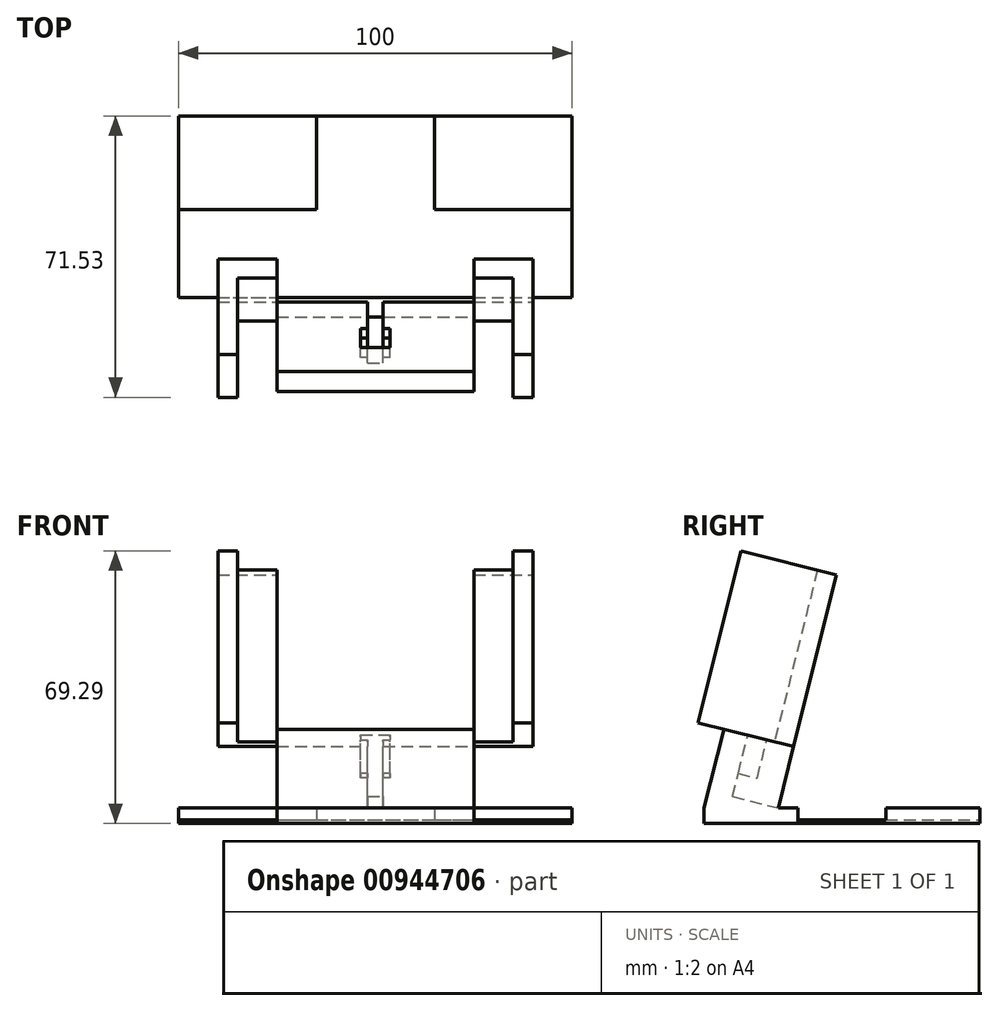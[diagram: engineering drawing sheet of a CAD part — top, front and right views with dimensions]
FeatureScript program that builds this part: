
annotation { "Feature Type Name" : "Feature", "Feature Type Description" : "" }
export const myFeature = defineFeature(function(context is Context, id is Id, definition is map)
    precondition{}
    {
        {
            var Q0;
            Q0=qCreatedBy(makeId("Top.planeOp"),FACE);
            var sketch = newSketch(context, id + "F0", { "sketchPlane" : qUnion([Q0])});
            skLineSegment(sketch, "E0.bottom", {"start": v(-50, 0) * mm, "end": v(50, 0) * mm});
            skLineSegment(sketch, "E0.top", {"start": v(-50, 70) * mm, "end": v(50, 70) * mm});
            skLineSegment(sketch, "E0.left", {"start": v(-50, 0) * mm, "end": v(-50, 70) * mm});
            skLineSegment(sketch, "E0.right", {"start": v(50, 0) * mm, "end": v(50, 70) * mm});
            skLineSegment(sketch, "E1.top", {"start": v(-15, 70) * mm, "end": v(15, 70) * mm});
            skLineSegment(sketch, "E1.left", {"start": v(-15, 46.16) * mm, "end": v(-15, 70) * mm});
            skLineSegment(sketch, "E1.right", {"start": v(15, 46.16) * mm, "end": v(15, 70) * mm});
            skLineSegment(sketch, "E2.bottom", {"start": v(-50, 46.16) * mm, "end": v(-15, 46.16) * mm});
            skLineSegment(sketch, "E2.top", {"start": v(-50, 23.84) * mm, "end": v(50, 23.84) * mm});
            skLineSegment(sketch, "E2.left", {"start": v(-50, 46.16) * mm, "end": v(-50, 23.84) * mm});
            skLineSegment(sketch, "E2.right", {"start": v(50, 46.16) * mm, "end": v(50, 23.84) * mm});
            skPoint(sketch, "E3", {"position": v(50, 35) * mm});
            skPoint(sketch, "E4", {"position": v(0, 70) * mm});
            skLineSegment(sketch, "E5.trimOffspring", {"start": v(15, 46.16) * mm, "end": v(50, 46.16) * mm});
            skLineSegment(sketch, "E6.bottom", {"start": v(-25, 0) * mm, "end": v(25, 0) * mm});
            skLineSegment(sketch, "E6.top", {"start": v(-25, 23.84) * mm, "end": v(25, 23.84) * mm});
            skLineSegment(sketch, "E6.left", {"start": v(-25, 0) * mm, "end": v(-25, 23.84) * mm});
            skLineSegment(sketch, "E6.right", {"start": v(25, 0) * mm, "end": v(25, 23.84) * mm});
            skSolve(sketch);
        }
        {
            var Q0;
            {var subQ0=sQuery(id+"F0.wireOp",EDGE,"E1.left");Q0=makeQuery(id+"F0.imprint","IMPRINT",FACE,{"disambiguationData":[TD([[makeQuery(id+"F0.imprint","IMPRINT",EDGE,{"derivedFrom":subQ0}),-1.0]])]});}
            extrude(context, id + "F1", {"entities" : qUnion([Q0]), "depth" : 1 * mm, "offsetDistance" : 25 * mm});
        }
        {
            var Q0;
            {var subQ0=sQuery(id+"F0.wireOp",EDGE,"E6.left");Q0=makeQuery(id+"F0.imprint","IMPRINT",FACE,{"disambiguationData":[TD([[makeQuery(id+"F0.imprint","IMPRINT",EDGE,{"derivedFrom":subQ0}),-1.0]])]});}
            var Q1;
            {var subQ0=sQuery(id+"F0.wireOp",EDGE,"E1.right");Q1=makeQuery(id+"F0.imprint","IMPRINT",FACE,{"disambiguationData":[TD([[makeQuery(id+"F0.imprint","IMPRINT",EDGE,{"derivedFrom":subQ0}),-1.0]])]});}
            var Q2;
            {var subQ3=sQuery(id+"F0.wireOp",EDGE,"E1.left");Q2=makeQuery(id+"F0.imprint","IMPRINT",FACE,{"disambiguationData":[TD([[makeQuery(id+"F0.imprint","IMPRINT",EDGE,{"derivedFrom":subQ3}),1.0]])]});}
            extrude(context, id + "F2", {"entities" : qUnion([Q0, Q1, Q2]), "operationType" : NewBodyOperationType.ADD, "depth" : 4 * mm, "offsetDistance" : 25 * mm});
        }
        {
            var Q0;
            Q0=makeQuery(id+"F2.opExtrude","CAP_FACE",FACE,{"disambiguationData":[OSD([sQuery(id+"F0.wireOp",EDGE,"E0.bottom"),sQuery(id+"F0.wireOp",EDGE,"E2.top"),sQuery(id+"F0.wireOp",EDGE,"E6.left"),sQuery(id+"F0.wireOp",EDGE,"E6.right")])],"isStart":false});
            var sketch = newSketch(context, id + "F3", { "sketchPlane" : qUnion([Q0])});
            skLineSegment(sketch, "E7.bottom", {"start": v(-25, 0) * mm, "end": v(25, 0) * mm});
            skLineSegment(sketch, "E7.top", {"start": v(-25, 18.84) * mm, "end": v(25, 18.84) * mm});
            skLineSegment(sketch, "E7.left", {"start": v(-25, 0) * mm, "end": v(-25, 18.84) * mm});
            skLineSegment(sketch, "E7.right", {"start": v(25, 0) * mm, "end": v(25, 18.84) * mm});
            skLineSegment(sketch, "E8.bottom", {"start": v(-25, 23.84) * mm, "end": v(25, 23.84) * mm});
            skLineSegment(sketch, "E8.top", {"start": v(-25, 5) * mm, "end": v(25, 5) * mm});
            skLineSegment(sketch, "E8.left", {"start": v(-25, 23.84) * mm, "end": v(-25, 5) * mm});
            skLineSegment(sketch, "E8.right", {"start": v(25, 23.84) * mm, "end": v(25, 5) * mm});
            skSolve(sketch);
        }
        {
            var Q0;
            {var subQ0=sQuery(id+"F3.wireOp",EDGE,"E7.top");Q0=makeQuery(id+"F3.imprint","IMPRINT",FACE,{"disambiguationData":[TD([[makeQuery(id+"F3.imprint","IMPRINT",EDGE,{"derivedFrom":subQ0}),1.0]])]});}
            var Q1;
            {var subQ0=sQuery(id+"F3.wireOp",EDGE,"E7.top");Q1=makeQuery(id+"F3.imprint","IMPRINT",FACE,{"disambiguationData":[TD([[makeQuery(id+"F3.imprint","IMPRINT",EDGE,{"derivedFrom":subQ0}),-1.0]])]});}
            var Q2;
            Q2=makeQuery(id+"F3.imprint","IMPRINT",FACE,{"disambiguationData":[TD([[makeQuery(id+"F3.imprint","IMPRINT",EDGE,{"derivedFrom":sQuery(id+"F3.wireOp",EDGE,"E7.bottom")}),1.0]])]});
            extrude(context, id + "F4", {"entities" : qUnion([Q0, Q1, Q2]), "operationType" : NewBodyOperationType.ADD, "depth" : 20 * mm, "offsetDistance" : 25 * mm});
        }
        {
            var Q0;
            Q0=makeQuery(id+"F4.boolean.opBoolean","MERGE",FACE,{"derivedFrom":[makeQuery(id+"F2.opExtrude","SWEPT_FACE",FACE,{"disambiguationData":[OSD([sQuery(id+"F0.wireOp",EDGE,"E6.right")])]}),makeQuery(id+"F4.opExtrude","SWEPT_FACE",FACE,{"disambiguationData":[OSD([sQuery(id+"F3.wireOp",EDGE,"E7.right"),sQuery(id+"F3.wireOp",EDGE,"E8.right")])]})]});
            var sketch = newSketch(context, id + "F5", { "sketchPlane" : qUnion([Q0])});
            skLineSegment(sketch, "E9.0", {"start": v(0, 4) * mm, "end": v(18.84, 4) * mm});
            skLineSegment(sketch, "E9.1", {"start": v(23.84, 4) * mm, "end": v(5, 4) * mm});
            skLineSegment(sketch, "E10", {"start": v(5, 4) * mm, "end": v(5, 24) * mm, "construction": true});
            skLineSegment(sketch, "E11", {"start": v(0, 4) * mm, "end": v(5, 24) * mm});
            skLineSegment(sketch, "E12", {"start": v(18.84, 4) * mm, "end": v(23.84, 24) * mm});
            skLineSegment(sketch, "E13", {"start": v(5, 24) * mm, "end": v(22.73, 19.57) * mm});
            skSolve(sketch);
        }
        {
            var Q0;
            {var subQ0=sQuery(id+"F5.wireOp",EDGE,"E11");Q0=makeQuery(id+"F5.imprint","IMPRINT",FACE,{"disambiguationData":[TD([[makeQuery(id+"F5.imprint","IMPRINT",EDGE,{"derivedFrom":subQ0}),1.0]])]});}
            var Q1;
            {var subQ0=sQuery(id+"F5.wireOp",EDGE,"E9.1");Q1=makeQuery(id+"F5.imprint","IMPRINT",FACE,{"disambiguationData":[TD([[makeQuery(id+"F5.imprint","IMPRINT",EDGE,{"derivedFrom":subQ0}),-1.0]])]});}
            var Q2;
            {var subQ6=sQuery(id+"F5.wireOp",EDGE,"E13");Q2=makeQuery(id+"F5.imprint","IMPRINT",FACE,{"disambiguationData":[TD([[makeQuery(id+"F5.imprint","IMPRINT",EDGE,{"derivedFrom":subQ6}),1.0]])]});}
            extrude(context, id + "F6", {"entities" : qUnion([Q0, Q1, Q2]), "operationType" : NewBodyOperationType.REMOVE, "oppositeDirection" : true, "depth" : 50 * mm, "offsetDistance" : 25 * mm});
        }
        {
            var Q0;
            Q0=makeQuery(id+"F6.boolean.opBoolean","COPY",FACE,{"derivedFrom":makeQuery(id+"F6.opExtrude","SWEPT_FACE",FACE,{"disambiguationData":[OSD([sQuery(id+"F5.wireOp",EDGE,"E12")])]})});
            var sketch = newSketch(context, id + "F7", { "sketchPlane" : qUnion([Q0])});
            skLineSegment(sketch, "E14.bottom", {"start": v(-3.75, 8.45) * mm, "end": v(3.75, 8.45) * mm});
            skLineSegment(sketch, "E14.top", {"start": v(-3.75, 24.5) * mm, "end": v(3.75, 24.5) * mm});
            skLineSegment(sketch, "E14.left", {"start": v(-3.75, 8.45) * mm, "end": v(-3.75, 24.5) * mm});
            skLineSegment(sketch, "E14.right", {"start": v(3.75, 8.45) * mm, "end": v(3.75, 24.5) * mm});
            skPoint(sketch, "E15", {"position": v(0, 8.45) * mm});
            skLineSegment(sketch, "E16.bottom", {"start": v(-2, 8.45) * mm, "end": v(2, 8.45) * mm});
            skLineSegment(sketch, "E16.top", {"start": v(-2, 24.5) * mm, "end": v(2, 24.5) * mm});
            skLineSegment(sketch, "E16.left", {"start": v(-2, 8.45) * mm, "end": v(-2, 24.5) * mm});
            skLineSegment(sketch, "E16.right", {"start": v(2, 8.45) * mm, "end": v(2, 24.5) * mm});
            skLineSegment(sketch, "E17.bottom", {"start": v(-3.75, 14.5) * mm, "end": v(3.75, 14.5) * mm});
            skLineSegment(sketch, "E17.left", {"start": v(-3.75, 14.5) * mm, "end": v(-3.75, 24.5) * mm});
            skLineSegment(sketch, "E17.right", {"start": v(3.75, 14.5) * mm, "end": v(3.75, 24.5) * mm});
            skSolve(sketch);
        }
        {
            var Q0;
            {var subQ0=sQuery(id+"F7.wireOp",EDGE,"E16.right");var subQ1=sQuery(id+"F7.wireOp",EDGE,"E14.top");var subQ2=makeQuery(id+"F7.imprint","INTERSECT",VERTEX,{"derivedFrom":[subQ1,subQ0]});Q0=makeQuery(id+"F7.imprint","IMPRINT",FACE,{"disambiguationData":[TD([[makeQuery(id+"F7.imprint","IMPRINT",EDGE,{"disambiguationData":[TD([[subQ2,-1.0]])],"derivedFrom":subQ1}),1.0]])]});}
            var Q1;
            {var subQ0=sQuery(id+"F7.wireOp",EDGE,"E16.right");var subQ1=sQuery(id+"F7.wireOp",EDGE,"E14.bottom");var subQ2=makeQuery(id+"F7.imprint","INTERSECT",VERTEX,{"derivedFrom":[subQ1,subQ0]});Q1=makeQuery(id+"F7.imprint","IMPRINT",FACE,{"disambiguationData":[TD([[makeQuery(id+"F7.imprint","IMPRINT",EDGE,{"disambiguationData":[TD([[subQ2,-1.0]])],"derivedFrom":subQ1}),-1.0]])]});}
            extrude(context, id + "F8", {"entities" : qUnion([Q0, Q1]), "operationType" : NewBodyOperationType.REMOVE, "oppositeDirection" : true, "depth" : 12 * mm, "offsetDistance" : 25 * mm});
        }
        {
            var Q0;
            {var subQ3=sQuery(id+"F7.wireOp",EDGE,"E16.right");var subQ5=sQuery(id+"F7.wireOp",EDGE,"E17.bottom");var subQ7=makeQuery(id+"F7.imprint","INTERSECT",VERTEX,{"derivedFrom":[subQ3,subQ5]});Q0=makeQuery(id+"F7.imprint","IMPRINT",FACE,{"disambiguationData":[TD([[makeQuery(id+"F7.imprint","IMPRINT",EDGE,{"disambiguationData":[TD([[subQ7,-1.0]])],"derivedFrom":subQ3}),-1.0]])]});}
            var Q1;
            {var subQ3=sQuery(id+"F7.wireOp",EDGE,"E16.left");var subQ5=sQuery(id+"F7.wireOp",EDGE,"E17.bottom");var subQ6=makeQuery(id+"F7.imprint","INTERSECT",VERTEX,{"derivedFrom":[subQ3,subQ5]});Q1=makeQuery(id+"F7.imprint","IMPRINT",FACE,{"disambiguationData":[TD([[makeQuery(id+"F7.imprint","IMPRINT",EDGE,{"disambiguationData":[TD([[subQ6,-1.0]])],"derivedFrom":subQ3}),1.0]])]});}
            extrude(context, id + "F9", {"entities" : qUnion([Q0, Q1]), "operationType" : NewBodyOperationType.REMOVE, "oppositeDirection" : true, "depth" : 12 * mm, "offsetDistance" : 25 * mm, "hasSecondDirection" : true, "secondDirectionOppositeDirection" : true, "secondDirectionDepth" : 7 * mm});
        }
        {
            var Q0;
            Q0=makeQuery(id+"F6.boolean.opBoolean","COPY",FACE,{"derivedFrom":makeQuery(id+"F6.opExtrude","SWEPT_FACE",FACE,{"disambiguationData":[OSD([sQuery(id+"F5.wireOp",EDGE,"E13")])]})});
            var sketch = newSketch(context, id + "F10", { "sketchPlane" : qUnion([Q0])});
            skPoint(sketch, "E18", {"position": v(0, 17.3) * mm});
            skLineSegment(sketch, "E19", {"start": v(-40, 17.3) * mm, "end": v(40, 17.3) * mm});
            skLineSegment(sketch, "E20", {"start": v(40, 17.3) * mm, "end": v(40, -7.7) * mm});
            skLineSegment(sketch, "E21", {"start": v(40, -7.7) * mm, "end": v(35, -7.7) * mm});
            skLineSegment(sketch, "E22", {"start": v(35, -7.7) * mm, "end": v(35, 12.3) * mm});
            skLineSegment(sketch, "E23", {"start": v(35, 12.3) * mm, "end": v(-35, 12.3) * mm});
            skLineSegment(sketch, "E24", {"start": v(-35, 12.3) * mm, "end": v(-35, -7.7) * mm});
            skLineSegment(sketch, "E25", {"start": v(-35, -7.7) * mm, "end": v(-40, -7.7) * mm});
            skLineSegment(sketch, "E26", {"start": v(-40, -7.7) * mm, "end": v(-40, 17.3) * mm});
            skSolve(sketch);
        }
        {
            var Q0;
            {var subQ1=sQuery(id+"F10.wireOp",EDGE,"E20");Q0=makeQuery(id+"F10.imprint","IMPRINT",FACE,{"disambiguationData":[TD([[makeQuery(id+"F10.imprint","IMPRINT",EDGE,{"derivedFrom":subQ1}),-1.0]])]});}
            var Q1;
            {var subQ0=sQuery(id+"F10.wireOp",EDGE,"E19");var subQ1=makeQuery(id+"F6.boolean.opBoolean","COPY",EDGE,{"derivedFrom":makeQuery(id+"F6.opExtrude","CAP_EDGE",EDGE,{"disambiguationData":[OSD([sQuery(id+"F5.wireOp",EDGE,"E13")])],"isStart":true})});var subQ2=makeQuery(id+"F10.imprint","INTERSECT",VERTEX,{"derivedFrom":[subQ1,subQ0]});Q1=makeQuery(id+"F10.imprint","IMPRINT",FACE,{"disambiguationData":[TD([[makeQuery(id+"F10.imprint","IMPRINT",EDGE,{"disambiguationData":[TD([[subQ2,1.0]])],"derivedFrom":subQ1}),1.0]])]});}
            var Q2;
            {var subQ0=sQuery(id+"F10.wireOp",EDGE,"E19");var subQ1=makeQuery(id+"F6.boolean.opBoolean","COPY",EDGE,{"derivedFrom":makeQuery(id+"F6.opExtrude","CAP_EDGE",EDGE,{"disambiguationData":[OSD([sQuery(id+"F5.wireOp",EDGE,"E13")])],"isStart":false})});var subQ2=makeQuery(id+"F10.imprint","INTERSECT",VERTEX,{"derivedFrom":[subQ1,subQ0]});Q2=makeQuery(id+"F10.imprint","IMPRINT",FACE,{"disambiguationData":[TD([[makeQuery(id+"F10.imprint","IMPRINT",EDGE,{"disambiguationData":[TD([[subQ2,1.0]])],"derivedFrom":subQ1}),-1.0]])]});}
            var Q3;
            {var subQ5=sQuery(id+"F10.wireOp",EDGE,"E24");Q3=makeQuery(id+"F10.imprint","IMPRINT",FACE,{"disambiguationData":[TD([[makeQuery(id+"F10.imprint","IMPRINT",EDGE,{"derivedFrom":subQ5}),-1.0]])]});}
            extrude(context, id + "F11", {"entities" : qUnion([Q0, Q1, Q2, Q3]), "operationType" : NewBodyOperationType.ADD, "depth" : 45 * mm, "offsetDistance" : 25 * mm});
        }
    });
